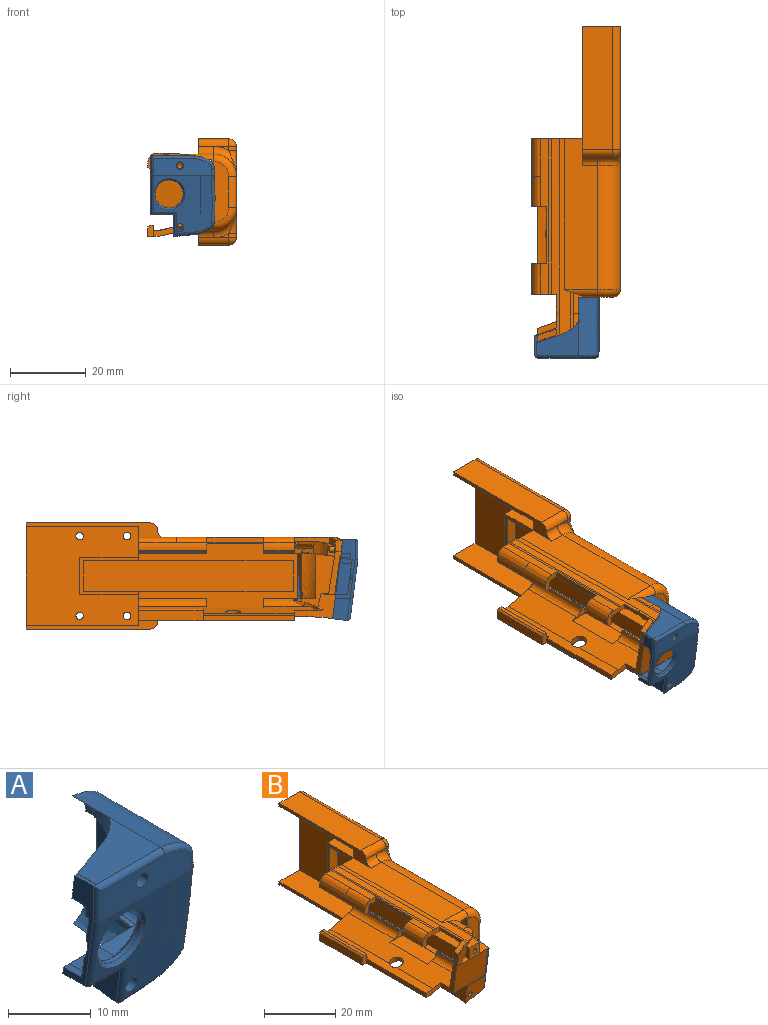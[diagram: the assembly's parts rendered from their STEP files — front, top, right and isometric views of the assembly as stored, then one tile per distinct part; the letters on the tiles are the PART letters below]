
ASSEMBLY  parts=2 mates=1
PART A: 77 faces, bbox 17.1x17.5x21.7 mm
  f0: cylinder r=0.75mm len=5.19mm, axis (0,0,1), area 5.8mm2, adj f3,f55,f56,f66,f69
  f1: plane 6.04x0.99mm, normal (0,0.99,0.13), area 6mm2, adj f11,f54,f56,f57,f76
  f2: plane 16.82x15.94mm, normal (0,0,-1), area 8.4mm2, adj f3,f10,f15,f16,f17,f28,f30,f42
  f3: plane 15.27x4.45mm, normal (0,-1,0), area 61.6mm2, adj f0,f2,f9,f67,f68,f69,f70,f71
  f4: plane 4x2.56mm, normal (-1,0,0), area 10.2mm2, adj f6,f7,f8,f10
  f5: plane 4x2.56mm, normal (1,0,0), area 10.2mm2, adj f6,f7,f8,f10
  f6: plane 4x2.56mm, normal (0,0,-1), area 10.2mm2, adj f4,f5,f8,f10
  f7: plane 4x2.56mm, normal (0,0,1), area 10.2mm2, adj f4,f5,f8,f10
  f8: plane 4x4mm, normal (0,1,0), area 12.9mm2, adj f4,f5,f6,f7,f9
  f9: cylinder r=1mm len=4.56mm, axis (0,-1,0), area 28.7mm2, adj f3,f8
  f10: plane 15.73x4.72mm, normal (0,1,0), area 22.2mm2, adj f2,f4,f5,f6,f7,f18,f19,f20
  f11: plane 6.79x4.58mm, normal (-1,0,0), area 21.5mm2, adj f1,f12,f35,f36,f51,f54,f57,f64
  f12: plane 5.02x3.21mm, normal (0.2,0.13,-0.97), area 15.9mm2, adj f11,f13,f36,f50
  f13: extruded ~3.19x2.05mm, area 7mm2, adj f12,f34,f36,f50
  f14: cylinder r=1mm len=4.82mm, axis (0,-0.99,-0.13), area 28.9mm2, adj f15,f36,f64
  f15: plane 15.38x15.38mm, normal (0,-0.99,-0.13), area 139mm2, adj f2,f14,f17,f52,f60,f61,f62,f63
  f16: plane 13.1x9.71mm, normal (0,0.99,0.13), area 69.4mm2, adj f2,f17,f35,f54,f56,f58,f72,f75
  f17: plane 9.91x2.79mm, normal (1,0,0), area 14.8mm2, adj f2,f15,f16,f52
  f18: plane 13.9x1.23mm, normal (0,0,-1), area 16.2mm2, adj f10,f19,f21,f27,f30
  f19: cylinder r=1mm len=13.9mm, axis (0,-1,0), area 21.3mm2, adj f10,f18,f20,f30,f42
  f20: plane 5.67x0.75mm, normal (-1,0,0), area 2.1mm2, adj f10,f19,f42
  f21: plane 11.05x0.17mm, normal (1,0,0), area 1.9mm2, adj f10,f18,f22
  f22: plane 11.03x3.76mm, normal (0,0,-1), area 29.9mm2, adj f10,f21,f23
  f23: plane 6.01x3.14mm, normal (-1,0,0), area 18.5mm2, adj f10,f22,f24
  f24: plane 5.76x4.2mm, normal (0,0,-1), area 19.6mm2, adj f10,f23,f25
  f25: plane 4.17x3.14mm, normal (1,0,0), area 12.5mm2, adj f10,f24,f31
  f26: extruded ~15.15x5.17mm, area 101.4mm2, adj f27,f29,f30,f33,f37,f71
  f27: extruded ~6.42x3.45mm, area 15.1mm2, adj f18,f26,f30
  f28: cylinder r=142.44mm len=15.15mm, axis (0,1,0), area 25.9mm2, adj f2,f29,f30,f37,f38,f68
  f29: plane 9.95x0.01mm, normal (1,0,0.04), area 0.1mm2, adj f26,f28,f37,f70
  f30: plane 19.22x5.58mm, normal (0,1,0), area 28.3mm2, adj f2,f18,f19,f26,f27,f28,f37,f38
  f31: plane 5.54x4.17mm, normal (0,0,-1), area 17.6mm2, adj f10,f25,f56,f59
  f32: plane 3.48x1.92mm, normal (-1,0,0), area 0.1mm2, adj f33,f55,f59,f69
  f33: plane 11.03x8.73mm, normal (0,0,1), area 59.4mm2, adj f26,f32,f69
  f34: plane 4.83x3.66mm, normal (1,0,0), area 13.8mm2, adj f13,f35,f36,f50
  f35: plane 7.06x3.07mm, normal (0,-0.13,0.99), area 21.9mm2, adj f11,f16,f34,f36,f58
  f36: plane 7.14x6.37mm, normal (0,0.99,0.13), area 36.4mm2, adj f11,f12,f13,f14,f34,f35
  f37: plane 5.77x0.82mm, normal (0,-0.13,0.99), area 0.2mm2, adj f26,f28,f29,f30,f38
  f38: plane 5.69x0.75mm, normal (1,0,0), area 2.1mm2, adj f28,f30,f37
  f39: plane 12.78x1.68mm, normal (0,-0.13,0.99), area 8.3mm2, adj f30,f40,f48,f50
  f40: extruded ~13.07x2.78mm, area 22.3mm2, adj f30,f39,f41,f50
  f41: plane 14.23x11.74mm, normal (-1,0,0), area 136.3mm2, adj f30,f40,f42,f50
  f42: plane 14.39x2.07mm, normal (-1,0,0.01), area 12.9mm2, adj f2,f19,f20,f30,f41,f50
  f43: cylinder r=140.11mm len=16.51mm, axis (0,0.99,0.13), area 169.2mm2, adj f2,f30,f44,f49,f61
  f44: extruded ~13.84x5.04mm, area 80.2mm2, adj f30,f43,f45,f51,f62
  f45: extruded ~13.16x4.72mm, area 51mm2, adj f30,f44,f46,f50
  f46: plane 12.76x1.71mm, normal (-1,-0.01,0.09), area 0.4mm2, adj f30,f45,f47,f50
  f47: plane 12.77x1.71mm, normal (-1,-0.01,0.08), area 0.4mm2, adj f30,f46,f48,f50
  f48: plane 12.78x1.82mm, normal (-1,-0.01,0.07), area 1.7mm2, adj f30,f39,f47,f50
  f49: plane 2.71x0.35mm, normal (1,0,0), area 0.5mm2, adj f2,f43,f60
  f50: plane 16x9.69mm, normal (0,0.99,0.13), area 35.5mm2, adj f2,f12,f13,f34,f39,f40,f41,f42
  f51: plane 5.69x0.82mm, normal (0.1,0.13,-0.99), area 4.3mm2, adj f11,f44,f50,f63
  f52: plane 9.91x2.79mm, normal (-1,0,0), area 14.8mm2, adj f2,f15,f17,f50
  f53: cylinder r=3.7mm len=7.42mm, axis (0,-0.99,-0.13), area 13.9mm2, adj f72,f73,f74
  f54: plane 5.04x3.09mm, normal (0,0,1), area 15.5mm2, adj f1,f11,f16,f58,f76
  f55: plane 3.23x0.5mm, normal (0,0,1), area 1.6mm2, adj f0,f32,f56,f59,f69
  f56: plane 15.52x5.21mm, normal (-1,0,0), area 24.4mm2, adj f0,f1,f2,f10,f16,f31,f55,f57
  f57: plane 6.04x3.94mm, normal (0,0,-1), area 23.8mm2, adj f1,f11,f56,f64,f65,f66
  f58: plane 2.92x0.38mm, normal (1,0,0), area 0.6mm2, adj f16,f35,f54
  f59: plane 3.62x0.61mm, normal (0,0.99,0.13), area 1.9mm2, adj f31,f32,f55,f56
  f60: cylinder r=0.75mm len=0.81mm, axis (0,-0.13,0.99), area 0.5mm2, adj f2,f15,f49,f61
  f61: bspline ~12.43x2.37mm, area 14.5mm2, adj f15,f43,f60,f62
  f62: bspline ~5.75x3.39mm, area 6.7mm2, adj f15,f44,f61,f63
  f63: cylinder r=0.75mm len=5.78mm, axis (0.99,-0.01,0.1), area 6.3mm2, adj f15,f51,f62,f64
  f64: cylinder r=0.75mm len=6.62mm, axis (0,0.13,-0.99), area 6.7mm2, adj f11,f14,f15,f57,f63,f65
  f65: cylinder r=0.75mm len=6.78mm, axis (1,0,0), area 6.5mm2, adj f15,f57,f64,f66
  f66: cylinder r=0.75mm len=10.53mm, axis (0,0.13,-0.99), area 11.7mm2, adj f0,f15,f56,f57,f65,f74
  f67: cylinder r=0.75mm len=0.04mm, axis (0,0,1), area 0mm2, adj f2,f3,f15
  f68: bspline ~4.07x0.92mm, area 2mm2, adj f2,f3,f28,f70
  f69: cylinder r=0.75mm len=11.53mm, axis (1,0,0), area 13.2mm2, adj f0,f3,f32,f33,f55,f71
  f70: cylinder r=0.75mm len=0.75mm, axis (0.04,0,-1), area 0mm2, adj f3,f29,f68,f71
  f71: bspline ~6x5.91mm, area 7.6mm2, adj f3,f26,f69,f70
  f72: cone r=4.15mm half-angle=45deg, axis (0,0.99,0.13), area 14.6mm2, adj f16,f53,f75
  f73: cone r=3.7mm half-angle=45deg, axis (0,-0.99,-0.13), area 14.6mm2, adj f15,f53,f74
  f74: bspline ~1.8x0.69mm, area 1.2mm2, adj f53,f66,f73
  f75: extruded ~3.31x1mm, area 3.4mm2, adj f16,f56,f72
  f76: plane 3.09x1mm, normal (0,0,1), area 3.1mm2, adj f1,f16,f54,f56
PART B: 199 faces, bbox 28.5x84.2x29.2 mm
  f0: plane 0.48x0.26mm, normal (0,-1,0), area 0.1mm2, adj f1,f2,f3,f4
  f1: cylinder r=0.75mm len=8.74mm, axis (0,1,0), area 10.3mm2, adj f0,f2,f4,f5,f6
  f2: cylinder r=2mm len=8.65mm, axis (1,0,0), area 16mm2, adj f0,f1,f3,f6,f7,f8,f9,f10
  f3: extruded ~5.28x3.74mm, area 21.8mm2, adj f0,f2,f10,f13,f14,f15,f16,f17
  f4: plane 8.74x1mm, normal (1,0,0), area 8.7mm2, adj f0,f1,f5,f16,f18
  f5: plane 6.68x2.5mm, normal (0,1,0), area 4.9mm2, adj f1,f4,f6,f15,f18,f19,f20,f21
  f6: plane 41.68x8.43mm, normal (0,0,-1), area 173.2mm2, adj f1,f2,f5,f11,f21,f22,f23,f24
  f7: torus R=4mm, axis (0,1,0), area 26mm2, adj f2,f12,f25,f26
  f8: plane 39.74x8.65mm, normal (0,0,1), area 315.7mm2, adj f2,f9,f24,f26,f27,f28
  f9: extruded ~51.76x3.05mm, area 92.1mm2, adj f2,f8,f10,f24,f29,f30
  f10: plane 9.76x0.63mm, normal (0.16,0,0.99), area 5.7mm2, adj f2,f3,f9,f17
  f11: plane 41.74x17mm, normal (-1,0,0), area 383.6mm2, adj f2,f6,f12,f24,f31,f32,f33,f34
  f12: plane 16x4.5mm, normal (0,-1,0), area 65.1mm2, adj f2,f7,f11,f25,f36,f37
  f13: plane 1.47x0.3mm, normal (0,0,-1), area 0mm2, adj f3,f38,f39
  f14: plane 0.97x0.07mm, normal (0,0,1), area 0mm2, adj f3,f39,f40
  f15: plane 9.95x1.5mm, normal (0,0,-1), area 5.4mm2, adj f3,f5,f16,f18,f19,f40
  f16: plane 1.53x1.02mm, normal (0,1,0), area 0.4mm2, adj f3,f4,f15,f18
  f17: extruded ~3.79x2.81mm, area 5.1mm2, adj f3,f10
  f18: cylinder r=0.75mm len=8.74mm, axis (0,1,0), area 10.3mm2, adj f4,f5,f15,f16
  f19: extruded ~13x2.43mm, area 35.8mm2, adj f5,f15,f20,f43,f44,f45
  f20: plane 8.74x0.59mm, normal (-0.13,0,-0.99), area 5.2mm2, adj f5,f19,f21,f45
  f21: extruded ~41.74x2.94mm, area 97mm2, adj f5,f6,f20,f22,f24,f45,f46,f47
  f22: plane 6.68x2.5mm, normal (0,-1,0), area 4.9mm2, adj f6,f21,f23,f46,f50,f51,f52,f53
  f23: cylinder r=0.75mm len=18mm, axis (0,1,0), area 21.2mm2, adj f6,f22,f24,f53
  f24: plane 21.43x9mm, normal (0,1,0), area 81.1mm2, adj f6,f8,f9,f11,f21,f23,f28,f29
  f25: cylinder r=2mm len=8mm, axis (0,0,-1), area 25.1mm2, adj f7,f12,f37,f70
  f26: cylinder r=6mm len=32.74mm, axis (0,1,0), area 308.6mm2, adj f7,f8,f70,f71
  f27: cylinder r=2mm len=4mm, axis (1,0,0), area 12.6mm2, adj f8,f28,f71,f72
  f28: plane 36.63x4mm, normal (-1,0,0), area 49.6mm2, adj f8,f24,f27,f69,f72,f73,f74
  f29: cylinder r=119.52mm len=46mm, axis (0,1,0), area 93.6mm2, adj f9,f24,f30,f48,f68,f75
  f30: cylinder r=117.91mm len=6.04mm, axis (0,1,0), area 4.6mm2, adj f9,f29,f75,f76,f77
  f31: plane 55.24x4.5mm, normal (0,0,-1), area 226.8mm2, adj f11,f24,f32,f56,f86,f87
  f32: plane 8x4.5mm, normal (0,1,0), area 36mm2, adj f11,f31,f33,f86
  f33: plane 55.24x4.5mm, normal (0,0,1), area 226.8mm2, adj f11,f32,f34,f56,f86,f87
  f34: plane 21.39x9mm, normal (0,1,0), area 80.6mm2, adj f11,f33,f35,f54,f56,f88,f89,f90
  f35: plane 41.68x1.75mm, normal (0,0,1), area 72.9mm2, adj f11,f34,f36,f105
  f36: cylinder r=2mm len=7.45mm, axis (-1,0,0), area 15.5mm2, adj f11,f12,f35,f37,f90,f91,f105,f107
  f37: torus R=4mm, axis (0,1,0), area 26mm2, adj f12,f25,f36,f109
  f38: plane 0.13x0.03mm, normal (-1,0,0), area 0mm2, adj f13,f42,f110
  f39: bspline ~4.65x1.32mm, area 0.8mm2, adj f13,f14,f40,f41,f110,f111
  f40: plane 12.03x2.17mm, normal (-0.49,0.87,0), area 15.6mm2, adj f14,f15,f39,f111,f112,f113,f114
  f41: plane 0.11x0.04mm, normal (0,0,-1), area 0mm2, adj f39,f42
  f42: cylinder r=9.39mm len=0.97mm, axis (0,-0.13,0.99), area 0.1mm2, adj f38,f41,f110
  f43: bspline ~3.04x1.71mm, area 0.9mm2, adj f19,f120
  f44: extruded ~6.3x5mm, area 30mm2, adj f19,f45,f48,f49,f75,f120,f121,f122
  f45: plane 4.39x1.59mm, normal (0,-1,0), area 1mm2, adj f19,f20,f21,f44,f49
  f46: plane 18x0.59mm, normal (-0.13,0,-0.99), area 10.8mm2, adj f21,f22,f24,f50
  f47: cylinder r=93.71mm len=41mm, axis (0,1,0), area 88.3mm2, adj f21,f24,f48,f57
  f48: plane 8.61x4.16mm, normal (0,-1,0), area 13.4mm2, adj f21,f29,f44,f47,f49,f57,f58,f67
  f49: plane 0.74x0.36mm, normal (-0.98,0,0.19), area 0.3mm2, adj f21,f44,f45,f48
  f50: extruded ~18x2.43mm, area 67.8mm2, adj f22,f24,f46,f51
  f51: plane 18x0.48mm, normal (0,0,-1), area 8.6mm2, adj f22,f24,f50,f52
  f52: cylinder r=0.75mm len=18mm, axis (0,1,0), area 21.2mm2, adj f22,f24,f51,f53
  f53: plane 18x1mm, normal (1,0,0), area 18mm2, adj f22,f23,f24,f52
  f54: plane 29.63x26mm, normal (-1,0,0), area 602.8mm2, adj f24,f34,f55,f69,f74,f88,f106,f135
  f55: plane 15.5x3mm, normal (0,0,1), area 46.5mm2, adj f24,f54,f56,f138
  f56: plane 15.5x10mm, normal (-1,0,0), area 39mm2, adj f24,f31,f33,f34,f55,f87,f106,f138
  f57: plane 41x0.62mm, normal (-0.03,0,-1), area 25.5mm2, adj f24,f47,f48,f58
  f58: cylinder r=53.77mm len=41mm, axis (0,1,0), area 63.6mm2, adj f24,f48,f57,f59,f127,f140,f141,f142
  f59: extruded ~10x0.6mm, area 8.5mm2, adj f24,f58,f60,f141
  f60: extruded ~18x1.32mm, area 24.3mm2, adj f24,f59,f61,f141,f142
  f61: plane 18x0.72mm, normal (1,0,0), area 12.9mm2, adj f24,f60,f62,f142
  f62: plane 18x1mm, normal (0,0,-1), area 18mm2, adj f24,f61,f63,f142
  f63: plane 18x0.5mm, normal (-0.71,0,-0.71), area 12.7mm2, adj f24,f62,f64,f142
  f64: plane 18x0.1mm, normal (-1,0,0), area 1.9mm2, adj f24,f63,f65,f142
  f65: cylinder r=3.64mm len=18mm, axis (0,1,0), area 38.2mm2, adj f24,f64,f66,f142,f144
  f66: extruded ~10x1.95mm, area 25.7mm2, adj f24,f65,f67,f144
  f67: cylinder r=57.51mm len=41mm, axis (0,1,0), area 64.9mm2, adj f24,f48,f66,f68,f134,f140,f142,f143
  f68: plane 41x0.64mm, normal (0.03,0,1), area 26.3mm2, adj f24,f29,f48,f67
  f69: plane 29.63x8mm, normal (0,0,-1), area 237mm2, adj f24,f28,f54,f74
  f70: plane 69.37x24mm, normal (1,0,0), area 1083.6mm2, adj f25,f26,f74,f109,f135,f136,f137,f139
  f71: torus R=8mm, axis (0,1,0), area 21.6mm2, adj f26,f27,f150,f151
  f72: cylinder r=2mm len=8mm, axis (1,0,0), area 25.1mm2, adj f27,f28,f73,f151,f152
  f73: plane 32.63x8mm, normal (0,0,1), area 261mm2, adj f28,f72,f74,f148
  f74: plane 28x10mm, normal (0,1,0), area 70.3mm2, adj f28,f54,f69,f70,f73,f88,f89,f147
  f75: plane 9.19x1.59mm, normal (-1,0,0), area 10.8mm2, adj f29,f30,f44,f48,f123,f124,f154
  f76: bspline ~4.94x3.26mm, area 7.9mm2, adj f30,f77,f84,f154
  f77: extruded ~5.11x1.98mm, area 1.4mm2, adj f30,f76,f84
  f78: plane 0.76x0.27mm, normal (0,0.13,-0.99), area 0.1mm2, adj f85,f155
  f79: plane 4.21x1.5mm, normal (0,-0.13,0.99), area 3.2mm2, adj f80,f155
  f80: plane 4x1.74mm, normal (-1,0,0), area 5.9mm2, adj f79,f81,f156,f157
  f81: plane 4x3.16mm, normal (0,0,1), area 8.4mm2, adj f80,f82,f157
  f82: plane 4x3.45mm, normal (1,0,0), area 12.5mm2, adj f81,f83,f156,f157
  f83: plane 6.51x3.87mm, normal (0,-0.13,0.99), area 19.3mm2, adj f82,f111,f155,f158,f159,f160,f161
  f84: plane 3.05x1.86mm, normal (-1,0,0.01), area 5mm2, adj f76,f77,f124,f154,f162,f163
  f85: plane 11.69x3.42mm, normal (-1,0,0), area 16.5mm2, adj f78,f125,f155,f162,f163
  f86: plane 55.24x8mm, normal (-1,0,0), area 441.9mm2, adj f31,f32,f33,f87
  f87: plane 8x3mm, normal (0,-1,0), area 24mm2, adj f31,f33,f56,f86
  f88: plane 29.63x8mm, normal (0,0,1), area 237mm2, adj f34,f54,f74,f89
  f89: plane 36.63x4mm, normal (-1,0,0), area 49.6mm2, adj f34,f74,f88,f90,f153,f164,f165
  f90: plane 39.74x7.45mm, normal (0,0,-1), area 268mm2, adj f34,f36,f89,f91,f109,f165
  f91: plane 46x7.48mm, normal (0.24,0,-0.97), area 247.4mm2, adj f34,f36,f90,f92,f108,f115,f166,f167
  f92: extruded ~41x2.8mm, area 116.6mm2, adj f34,f91,f93,f167,f168
  f93: plane 41x1.63mm, normal (0,0,-1), area 30.9mm2, adj f34,f92,f94,f167,f169,f170
  f94: plane 17x2.6mm, normal (-1,0,0), area 44.2mm2, adj f34,f93,f95,f170
  f95: plane 17x0.5mm, normal (-0.71,0,0.71), area 12mm2, adj f34,f94,f96,f170
  f96: plane 17x1mm, normal (0,0,1), area 17mm2, adj f34,f95,f97,f170
  f97: plane 17x1.05mm, normal (1,0,0), area 17.9mm2, adj f34,f96,f98,f170
  f98: cylinder r=0.5mm len=17mm, axis (0,1,0), area 14.3mm2, adj f34,f97,f99,f170
  f99: extruded ~41x2.56mm, area 95.9mm2, adj f34,f98,f100,f167,f168,f169,f170
  f100: plane 46.03x7.53mm, normal (-0.24,0,0.97), area 302.5mm2, adj f34,f99,f101,f115,f117,f119,f167,f168
  f101: extruded ~18x2.06mm, area 54.4mm2, adj f34,f100,f102,f173
  f102: plane 18x0.25mm, normal (0,0,1), area 4.5mm2, adj f34,f101,f103,f173
  f103: cylinder r=0.75mm len=18mm, axis (0,1,0), area 21.2mm2, adj f34,f102,f104,f173
  f104: plane 18x1mm, normal (1,0,0), area 18mm2, adj f34,f103,f105,f173
  f105: cylinder r=0.75mm len=41.74mm, axis (0,1,0), area 31.7mm2, adj f34,f35,f36,f104,f107,f171,f172,f173
  f106: plane 15.5x3mm, normal (0,0,-1), area 46.5mm2, adj f34,f54,f56,f138
  f107: plane 0.37x0.24mm, normal (0,-1,0), area 0mm2, adj f36,f105,f108,f175
  f108: extruded ~4.83x3.23mm, area 9.1mm2, adj f36,f91,f107,f176,f177
  f109: cylinder r=6mm len=32.74mm, axis (0,1,0), area 308.6mm2, adj f37,f70,f90,f178
  f110: plane 0.95x0.32mm, normal (0,0,1), area 0mm2, adj f38,f39,f42
  f111: plane 4.71x1.41mm, normal (0,0,1), area 0.5mm2, adj f39,f40,f83,f113
  f112: bspline ~12x3.92mm, area 54.6mm2, adj f40
  f113: bspline ~11.83x4.71mm, area 33.1mm2, adj f40,f111,f114,f158,f179,f180
  f114: plane 13.73x2.77mm, normal (0,0,1), area 6.1mm2, adj f40,f113,f119,f171,f176,f181,f182
  f115: plane 10.93x6.59mm, normal (-1,0,0), area 34.9mm2, adj f91,f100,f125,f166,f167,f174,f183,f184
  f116: plane 1.44x0.95mm, normal (-0.34,0.91,0.22), area 1mm2, adj f117,f174,f188
  f117: bspline ~4.02x3.23mm, area 4.4mm2, adj f100,f116,f118,f119,f174
  f118: bspline ~3.35x1.7mm, area 1.5mm2, adj f117,f119
  f119: extruded ~11.42x2.06mm, area 28.3mm2, adj f100,f114,f117,f118,f171
  f120: plane 0.87x0.83mm, normal (0,1,0), area 0.3mm2, adj f43,f44
  f121: bspline ~0.76x0.4mm, area 0.1mm2, adj f44,f122
  f122: bspline ~1.6x1.41mm, area 0.7mm2, adj f44,f121,f123,f126
  f123: bspline ~5.44x5.36mm, area 12.7mm2, adj f44,f75,f122,f124,f126
  f124: bspline ~7.62x5.83mm, area 2.9mm2, adj f75,f84,f123,f154
  f125: plane 5.38x3.62mm, normal (0.05,0,-1), area 8.9mm2, adj f85,f115,f187
  f126: plane 5.05x0.87mm, normal (0,1,0), area 0.8mm2, adj f44,f122,f123
  f127: extruded ~8x0.6mm, area 6.8mm2, adj f48,f58,f128,f140
  f128: extruded ~8x1.32mm, area 10.8mm2, adj f48,f127,f129,f140
  f129: plane 8x0.72mm, normal (1,0,0), area 5.7mm2, adj f48,f128,f130,f140
  f130: plane 8x1mm, normal (0,0,-1), area 8mm2, adj f48,f129,f131,f140
  f131: plane 8x0.5mm, normal (-0.71,0,-0.71), area 5.7mm2, adj f48,f130,f132,f140
  f132: plane 8x0.1mm, normal (-1,0,0), area 0.8mm2, adj f48,f131,f133,f140
  f133: cylinder r=3.64mm len=8mm, axis (0,1,0), area 17mm2, adj f48,f132,f134,f140
  f134: extruded ~8x1.95mm, area 20.5mm2, adj f48,f67,f133,f140
  f135: cylinder r=1mm len=2mm, axis (-1,0,0), area 12.6mm2, adj f54,f70
  f136: cylinder r=1mm len=2mm, axis (-1,0,0), area 12.6mm2, adj f54,f70
  f137: cylinder r=1mm len=2mm, axis (-1,0,0), area 12.6mm2, adj f54,f70
  f138: plane 10x3mm, normal (0,1,0), area 30mm2, adj f54,f55,f56,f106
  f139: cylinder r=1mm len=2mm, axis (-1,0,0), area 12.6mm2, adj f54,f70
  f140: plane 4.16x4.04mm, normal (0,1,0), area 8.8mm2, adj f58,f67,f127,f128,f129,f130,f131,f132
  f141: extruded ~8x0.6mm, area 6.8mm2, adj f58,f59,f60,f142
  f142: plane 4.16x4.04mm, normal (0,-1,0), area 8.8mm2, adj f58,f60,f61,f62,f63,f64,f65,f67
  f143: plane 15x1.52mm, normal (-1,0,0), area 22.8mm2, adj f58,f67,f140,f142
  f144: extruded ~8x1.95mm, area 20.5mm2, adj f65,f66,f67,f142
  f145: bspline ~8.01x4mm, area 8.3mm2, adj f70,f146,f178
  f146: cylinder r=2mm len=2mm, axis (0,0,-1), area 3.4mm2, adj f70,f145,f190,f191
  f147: cylinder r=2mm len=32.63mm, axis (0,-1,0), area 102.5mm2, adj f70,f74,f153,f190
  f148: cylinder r=2mm len=32.63mm, axis (0,-1,0), area 102.5mm2, adj f70,f73,f74,f152
  f149: cylinder r=2mm len=2mm, axis (0,0,1), area 3.4mm2, adj f70,f150,f151,f152
  f150: bspline ~8.01x4mm, area 8.3mm2, adj f70,f71,f149
  f151: plane 4x1.07mm, normal (0,-1,0), area 1.4mm2, adj f71,f72,f149
  f152: sphere r=2mm, area 4mm2, adj f72,f148,f149
  f153: plane 32.63x8mm, normal (0,0,-1), area 261mm2, adj f74,f89,f147,f164
  f154: extruded ~5.38x2.35mm, area 8.2mm2, adj f75,f76,f84,f124
  f155: plane 12.59x9.91mm, normal (0,-0.99,-0.13), area 124.4mm2, adj f78,f79,f83,f85,f156,f161,f186,f187
  f156: plane 4x0.25mm, normal (0,0.13,-0.99), area 1mm2, adj f80,f82,f155,f157
  f157: plane 4x4mm, normal (0,-1,0), area 14.2mm2, adj f80,f81,f82,f156,f193
  f158: plane 1.23x0.85mm, normal (0,0.21,0.98), area 0.5mm2, adj f83,f113,f180
  f159: plane 14.64x10.31mm, normal (1,0,0), area 87.5mm2, adj f83,f160,f177,f180,f194
  f160: cylinder r=0.4mm len=14.39mm, axis (0,-0.13,0.99), area 8.9mm2, adj f83,f159,f161,f177,f185
  f161: plane 9.95x1.55mm, normal (-1,0,0), area 2.5mm2, adj f83,f155,f160,f186
  f162: plane 0.24x0.01mm, normal (-0.32,0.95,0), area 0mm2, adj f84,f85,f163
  f163: plane 1.55x0.23mm, normal (0.1,0.14,-0.98), area 0mm2, adj f84,f85,f162
  f164: cylinder r=2mm len=8mm, axis (-1,0,0), area 25.1mm2, adj f89,f153,f165,f190,f191
  f165: cylinder r=2mm len=4mm, axis (-1,0,0), area 12.6mm2, adj f89,f90,f164,f178
  f166: plane 4.87x1.3mm, normal (0.24,0.1,-0.97), area 4.2mm2, adj f91,f115,f189
  f167: plane 5.4x2.6mm, normal (0,-1,0), area 8.3mm2, adj f91,f92,f93,f99,f100,f115,f169
  f168: cylinder r=2mm len=4.24mm, axis (-0.24,0,0.97), area 18.8mm2, adj f91,f92,f99,f100
  f169: plane 24x1.49mm, normal (-1,0,0), area 35.9mm2, adj f93,f99,f167,f170
  f170: plane 3.1x2.06mm, normal (0,-1,0), area 4.6mm2, adj f93,f94,f95,f96,f97,f98,f99,f169
  f171: plane 5.19x2.5mm, normal (0,1,0), area 4.5mm2, adj f100,f105,f114,f119,f172,f175,f181
  f172: plane 15x5.19mm, normal (0.01,0,1), area 77.8mm2, adj f100,f105,f171,f173
  f173: plane 5.19x2.5mm, normal (0,-1,0), area 4.5mm2, adj f100,f101,f102,f103,f104,f105,f172
  f174: plane 2.79x2.7mm, normal (-0.24,0.1,0.97), area 1.7mm2, adj f100,f115,f116,f117,f188
  f175: plane 8.74x1mm, normal (1,0,0), area 8.7mm2, adj f105,f107,f171,f176,f181
  f176: plane 1.64x1.11mm, normal (0,1,0), area 0.5mm2, adj f108,f114,f175,f181,f182
  f177: extruded ~9.06x2.53mm, area 20.5mm2, adj f108,f159,f160,f184,f185
  f178: torus R=8mm, axis (0,1,0), area 21.6mm2, adj f109,f145,f165,f191
  f179: plane 2.96x2.02mm, normal (0,0.21,-0.98), area 2.6mm2, adj f113,f180,f194
  f180: plane 10.92x3.76mm, normal (0.98,0.21,0), area 18.5mm2, adj f113,f158,f159,f179
  f181: cylinder r=0.75mm len=8.74mm, axis (0,1,0), area 10.3mm2, adj f114,f171,f175,f176
  f182: plane 0.23x0.02mm, normal (1,0,-0.06), area 0mm2, adj f114,f176
  f183: bspline ~4.93x2.52mm, area 0mm2, adj f115,f184,f189,f195
  f184: plane 5.37x5.02mm, normal (0.2,0.13,-0.97), area 19.7mm2, adj f115,f177,f183,f185,f195
  f185: plane 7.16x6.37mm, normal (0,-0.99,-0.13), area 37.8mm2, adj f115,f160,f177,f184,f186,f196
  f186: plane 7.06x0.25mm, normal (0,-0.13,0.99), area 1.8mm2, adj f115,f155,f161,f185
  f187: plane 5.38x1.95mm, normal (0,0.13,-0.99), area 5.3mm2, adj f115,f125,f155
  f188: plane 1.62x0.6mm, normal (-0.99,0.05,-0.15), area 0.5mm2, adj f115,f116,f174
  f189: extruded ~4.35x3.11mm, area 2.8mm2, adj f115,f166,f183,f195
  f190: sphere r=2mm, area 8.6mm2, adj f146,f147,f164
  f191: plane 4x1.07mm, normal (0,-1,0), area 1.4mm2, adj f146,f164,f178
  f192: plane 0.16x0.05mm, normal (0,0.13,-0.99), area 0mm2, adj f155
  f193: cylinder r=0.75mm len=3mm, axis (0,-1,0), area 14.1mm2, adj f157,f197
  f194: plane 3.05x1.99mm, normal (0,-0.13,0.99), area 2.6mm2, adj f159,f179
  f195: plane 0.28x0.24mm, normal (-0.3,0,0.95), area 0mm2, adj f183,f184,f189
  f196: cylinder r=0.75mm len=2.67mm, axis (0,-0.99,-0.13), area 11.8mm2, adj f185,f198
  f197: cone r=0.75mm half-angle=59deg, axis (0,-1,0), area 2.1mm2, adj f193
  f198: cone r=0.75mm half-angle=59deg, axis (0,-0.99,-0.13), area 2.1mm2, adj f196
PLACE A t=(0.75,-18.62,0.02)mm
PLACE B at identity
MATE fastened A.f9 <-> B.f193  axis (0,1,0) through (-0.02,-22.15,7.8)mm
